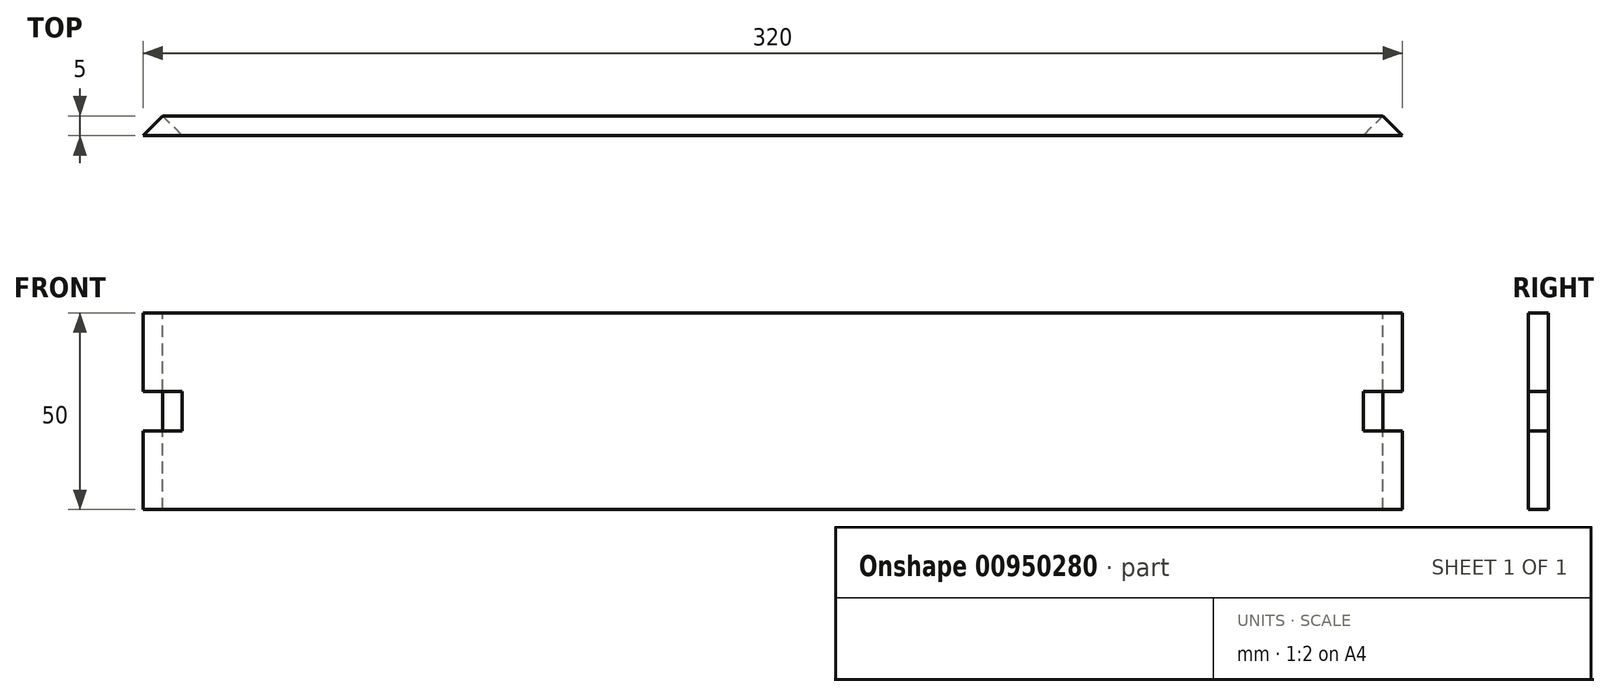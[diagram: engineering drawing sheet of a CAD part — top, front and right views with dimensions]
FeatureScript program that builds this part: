
annotation { "Feature Type Name" : "Feature", "Feature Type Description" : "" }
export const myFeature = defineFeature(function(context is Context, id is Id, definition is map)
    precondition{}
    {
        {
            var Q0;
            Q0=qCreatedBy(makeId("Front.planeOp"),FACE);
            var sketch = newSketch(context, id + "F0", { "sketchPlane" : qUnion([Q0])});
            skLineSegment(sketch, "E0.bottom", {"start": v(160, -25) * mm, "end": v(-160, -25) * mm});
            skLineSegment(sketch, "E0.top", {"start": v(160, 25) * mm, "end": v(-160, 25) * mm});
            skLineSegment(sketch, "E0.left", {"start": v(160, -25) * mm, "end": v(160, 25) * mm});
            skLineSegment(sketch, "E0.right", {"start": v(-160, -25) * mm, "end": v(-160, 25) * mm});
            skPoint(sketch, "E0.middle", {"position": v(0, 0) * mm});
            skSolve(sketch);
        }
        {
            var Q0;
            Q0=makeQuery(id+"F0.imprint","IMPRINT",FACE,{"disambiguationData":[TD([[makeQuery(id+"F0.imprint","IMPRINT",EDGE,{"derivedFrom":sQuery(id+"F0.wireOp",EDGE,"E0.bottom")}),-1.0]])]});
            extrude(context, id + "F1", {"entities" : qUnion([Q0]), "endBound" : BoundingType.SYMMETRIC, "depth" : 5 * mm, "offsetDistance" : 25 * mm});
        }
        {
            var Q0;
            Q0=makeQuery(id+"F1.opExtrude","SWEPT_FACE",FACE,{"disambiguationData":[OSD([sQuery(id+"F0.wireOp",EDGE,"E0.top")])]});
            var sketch = newSketch(context, id + "F2", { "sketchPlane" : qUnion([Q0])});
            skLineSegment(sketch, "E1", {"start": v(160, -2.5) * mm, "end": v(160, 2.5) * mm});
            skLineSegment(sketch, "E2", {"start": v(160, 2.5) * mm, "end": v(155, 2.5) * mm});
            skLineSegment(sketch, "E3", {"start": v(160, -2.5) * mm, "end": v(155, 2.5) * mm});
            skSolve(sketch);
        }
        {
            var Q0;
            Q0=makeQuery(id+"F2.imprint","IMPRINT",FACE,{"disambiguationData":[TD([[makeQuery(id+"F2.imprint","IMPRINT",EDGE,{"derivedFrom":sQuery(id+"F2.wireOp",EDGE,"E1")}),1.0]])]});
            extrude(context, id + "F3", {"entities" : qUnion([Q0]), "operationType" : NewBodyOperationType.REMOVE, "oppositeDirection" : true, "depth" : 50 * mm, "offsetDistance" : 25 * mm});
        }
        {
            var Q0;
            Q0=makeQuery(id+"F1.opExtrude","SWEPT_FACE",FACE,{"disambiguationData":[OSD([sQuery(id+"F0.wireOp",EDGE,"E0.top")])]});
            var sketch = newSketch(context, id + "F4", { "sketchPlane" : qUnion([Q0])});
            skLineSegment(sketch, "E4", {"start": v(-160, 2.5) * mm, "end": v(-160, -2.5) * mm});
            skLineSegment(sketch, "E5", {"start": v(-160, 2.5) * mm, "end": v(-155, 2.5) * mm});
            skLineSegment(sketch, "E6", {"start": v(-155, 2.5) * mm, "end": v(-160, -2.5) * mm});
            skSolve(sketch);
        }
        {
            var Q0;
            Q0=makeQuery(id+"F4.imprint","IMPRINT",FACE,{"disambiguationData":[TD([[makeQuery(id+"F4.imprint","IMPRINT",EDGE,{"derivedFrom":sQuery(id+"F4.wireOp",EDGE,"E4")}),-1.0]])]});
            extrude(context, id + "F5", {"entities" : qUnion([Q0]), "operationType" : NewBodyOperationType.REMOVE, "oppositeDirection" : true, "depth" : 60 * mm, "offsetDistance" : 25 * mm});
        }
        {
            var Q0;
            Q0=makeQuery(id+"F3.boolean.opBoolean","COPY",FACE,{"derivedFrom":makeQuery(id+"F3.opExtrude","SWEPT_FACE",FACE,{"disambiguationData":[OSD([sQuery(id+"F2.wireOp",EDGE,"E3")])]})});
            var sketch = newSketch(context, id + "F6", { "sketchPlane" : qUnion([Q0])});
            skLineSegment(sketch, "E7", {"start": v(-107.83, 0) * mm, "end": v(-114.9, 0) * mm});
            skLineSegment(sketch, "E8.bottom", {"start": v(-107.83, -5) * mm, "end": v(-114.9, -5) * mm});
            skLineSegment(sketch, "E8.top", {"start": v(-107.83, 5) * mm, "end": v(-114.9, 5) * mm});
            skLineSegment(sketch, "E8.left", {"start": v(-107.83, -5) * mm, "end": v(-107.83, 5) * mm});
            skLineSegment(sketch, "E8.right", {"start": v(-114.9, -5) * mm, "end": v(-114.9, 5) * mm});
            skPoint(sketch, "E8.middle", {"position": v(-111.37, 0) * mm});
            skSolve(sketch);
        }
        {
            var Q0;
            Q0 = qSketchRegion(id + "F6", true);
            extrude(context, id + "F7", {"entities" : qUnion([Q0]), "operationType" : NewBodyOperationType.REMOVE, "oppositeDirection" : true, "depth" : 25 * mm, "offsetDistance" : 25 * mm});
        }
        {
            var Q0;
            Q0=makeQuery(id+"F5.boolean.opBoolean","COPY",FACE,{"derivedFrom":makeQuery(id+"F5.opExtrude","SWEPT_FACE",FACE,{"disambiguationData":[OSD([sQuery(id+"F4.wireOp",EDGE,"E6")])]})});
            var sketch = newSketch(context, id + "F8", { "sketchPlane" : qUnion([Q0])});
            skLineSegment(sketch, "E9", {"start": v(114.9, 0) * mm, "end": v(107.83, 0) * mm});
            skLineSegment(sketch, "E10.bottom", {"start": v(114.9, -5) * mm, "end": v(107.83, -5) * mm});
            skLineSegment(sketch, "E10.top", {"start": v(114.9, 5) * mm, "end": v(107.83, 5) * mm});
            skLineSegment(sketch, "E10.left", {"start": v(114.9, -5) * mm, "end": v(114.9, 5) * mm});
            skLineSegment(sketch, "E10.right", {"start": v(107.83, -5) * mm, "end": v(107.83, 5) * mm});
            skPoint(sketch, "E10.middle", {"position": v(111.37, 0) * mm});
            skSolve(sketch);
        }
        {
            var Q0;
            Q0 = qSketchRegion(id + "F8", true);
            extrude(context, id + "F9", {"entities" : qUnion([Q0]), "operationType" : NewBodyOperationType.REMOVE, "oppositeDirection" : true, "depth" : 25 * mm, "offsetDistance" : 25 * mm});
        }
    });
